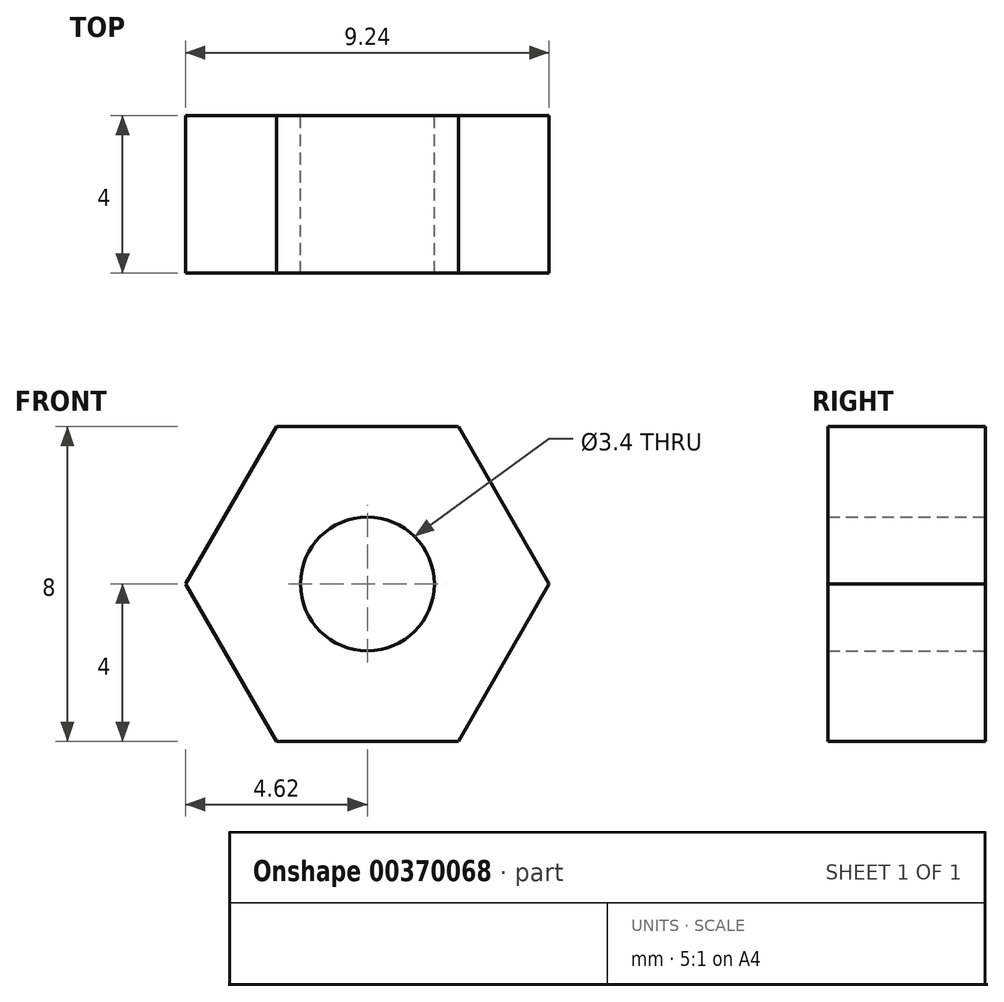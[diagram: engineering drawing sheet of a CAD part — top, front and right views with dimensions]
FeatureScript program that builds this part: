
annotation { "Feature Type Name" : "Feature", "Feature Type Description" : "" }
export const myFeature = defineFeature(function(context is Context, id is Id, definition is map)
    precondition{}
    {
        {
            var Q0;
            Q0=qCreatedBy(makeId("Front.planeOp"),FACE);
            var sketch = newSketch(context, id + "F0", { "sketchPlane" : qUnion([Q0])});
            skCircle(sketch, "E0", {"center": v(0, 4) * mm, "radius": 1.7 * mm});
            skPoint(sketch, "E0.centerSnap0", {"position": v(0, 4) * mm});
            skPoint(sketch, "E0.centerSnap1", {"position": v(0, 0) * mm});
            skPoint(sketch, "E1.orphan", {"position": v(0, 8) * mm});
            skCircle(sketch, "E2.cCircle", {"center": v(0, 4) * mm, "radius": 4 * mm, "construction": true});
            skLineSegment(sketch, "E2.0", {"start": v(-2.3, 8) * mm, "end": v(2.3, 8) * mm});
            skLineSegment(sketch, "E2.1", {"start": v(2.3, 8) * mm, "end": v(4.62, 4) * mm});
            skLineSegment(sketch, "E2.2", {"start": v(4.62, 4) * mm, "end": v(2.3, 0) * mm});
            skLineSegment(sketch, "E2.3", {"start": v(2.3, 0) * mm, "end": v(-2.3, 0) * mm});
            skLineSegment(sketch, "E2.4", {"start": v(-2.3, 0) * mm, "end": v(-4.62, 4) * mm});
            skLineSegment(sketch, "E2.5", {"start": v(-4.62, 4) * mm, "end": v(-2.3, 8) * mm});
            skSolve(sketch);
        }
        {
            var Q0;
            Q0 = qSketchRegion(id + "F0", true);
            extrude(context, id + "F1", {"entities" : qUnion([Q0]), "depth" : 4 * mm});
        }
    });
